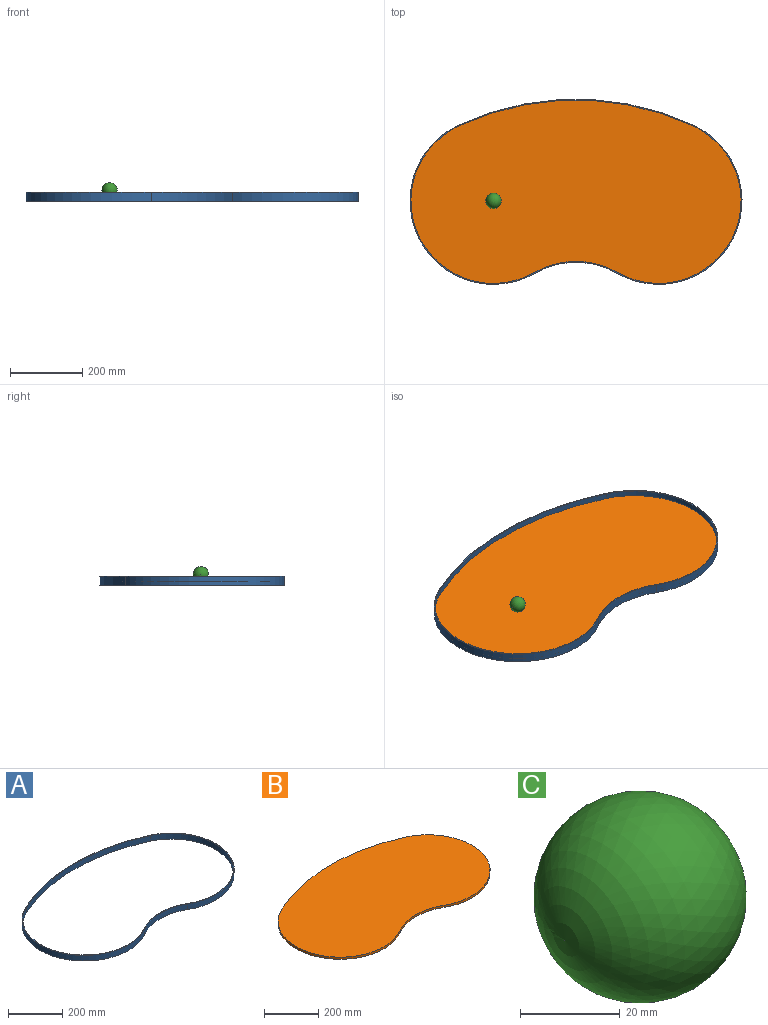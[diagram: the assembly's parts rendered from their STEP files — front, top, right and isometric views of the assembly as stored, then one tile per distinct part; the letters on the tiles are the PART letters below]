
ASSEMBLY  parts=3 mates=2
PART A: 10 faces, bbox 919.5x513.1x25.4 mm
  f0: cylinder r=770.89mm len=652.99mm, axis (0,0,-1), area 17126.7mm2, adj f1,f7,f8,f9
  f1: cylinder r=231.14mm len=440.53mm, axis (0,0,-1), area 18950.6mm2, adj f0,f2,f8,f9
  f2: cylinder r=226.06mm len=226.06mm, axis (0,0,-1), area 6012.9mm2, adj f1,f7,f8,f9
  f3: cylinder r=768.35mm len=650.84mm, axis (0,0,-1), area 17070.3mm2, adj f4,f6,f8,f9
  f4: cylinder r=228.6mm len=435.68mm, axis (0,0,-1), area 18742.3mm2, adj f3,f5,f8,f9
  f5: cylinder r=228.6mm len=228.6mm, axis (0,0,-1), area 6080.5mm2, adj f4,f6,f8,f9
  f6: cylinder r=228.6mm len=435.68mm, axis (0,0,-1), area 18742.3mm2, adj f3,f5,f8,f9
  f7: cylinder r=231.14mm len=440.53mm, axis (0,0,-1), area 18950.6mm2, adj f0,f2,f8,f9
  f8: plane 919.48x513.08mm, normal (0,0,1), area 6083.8mm2, adj f0,f1,f2,f3,f4,f5,f6,f7
  f9: plane 919.48x513.08mm, normal (0,0,-1), area 6083.8mm2, adj f0,f1,f2,f3,f4,f5,f6,f7
PART B: 6 faces, bbox 914.4x508x9.5 mm
  f0: cylinder r=228.6mm len=228.6mm, axis (0,0,-1), area 2280.2mm2, adj f1,f3,f4,f5
  f1: cylinder r=228.6mm len=435.68mm, axis (0,0,-1), area 7028.4mm2, adj f0,f2,f4,f5
  f2: cylinder r=768.35mm len=650.84mm, axis (0,0,-1), area 6401.3mm2, adj f1,f3,f4,f5
  f3: cylinder r=228.6mm len=435.68mm, axis (0,0,-1), area 7028.4mm2, adj f0,f2,f4,f5
  f4: plane 914.4x508mm, normal (0,0,1), area 378245.9mm2, adj f0,f1,f2,f3
  f5: plane 914.4x508mm, normal (0,0,-1), area 378245.9mm2, adj f0,f1,f2,f3
PART C: 1 faces, bbox 42.7x42.7x42.7 mm
  f0: sphere r=21.34mm, area 5720.5mm2
PLACE A at identity
PLACE B at identity fixed
PLACE C t=(-228.6,0,30.86)mm
MATE fastened A.f9 <-> B.f5  axis (0,0,-1) through (114.3,-197.97,0)mm
MATE fastened B.f3 <-> C.f0  axis (0,0,1) through (-228.6,0,9.52)mm
